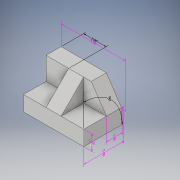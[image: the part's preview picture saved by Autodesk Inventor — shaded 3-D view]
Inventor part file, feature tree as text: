
AUTODESK INVENTOR PART (.ipt)
format: ipt  version: 2018 (Build 220112000, 112)  size: 166,400 bytes
history: native  units: in
note: dims shown in document units (in); Inventor stores cm internally (conversion verified against a paired STEP export)
features: other x7, sketch x6, extrude x3, chamfer x2
ambient origin geometry x8: Origin, YZ Plane, XZ Plane, XY Plane, X Axis, Y Axis, Z Axis, Center Point
bodies: Solid1 (feature_tree)
feature tree (18):
  other  "Annotations"
  extrude  "Extrusion1"  Depth=5.0in
  extrude  "Extrusion2"  Depth=2.0in
  chamfer  "Chamfer1"  Distance=3.0in
  extrude  "Extrusion3"  Depth=2.0in
  chamfer  "Chamfer2"  Distance=3.0in
  sketch  "Sketch4"  dims[d11=3.0in]
  sketch  "Sketch5"  dims[d12=3.0in]
  sketch  "Sketch6"  dims[d13=8.0in d14=3.0in d15=0.0in d16=3.0in d17=0.125in d18=45.0deg d20=8.0in d21=3.0in d23=2.0in d24=5.0in d26=2.0in d27=0.3937in d28=0.0244in d29=90.0deg]
  sketch  "Sketch1"  dims[d0=8.0in d1=5.0in]
  sketch  "Sketch2"  dims[d2=2.0in d3=0.0in d4=2.0in d5=3.0in d6=0.0in]
  sketch  "Sketch3"  dims[d7=2.0in d8=0.125in d9=0.3869in d10=2.0in]
  other  "Linear Dimension 2"
  other  "Linear Dimension 3"
  other  "Linear Dimension 4"
  other  "Linear Dimension 5"
  other  "Linear Dimension 6"
  other  "Angular Dimension 1"
